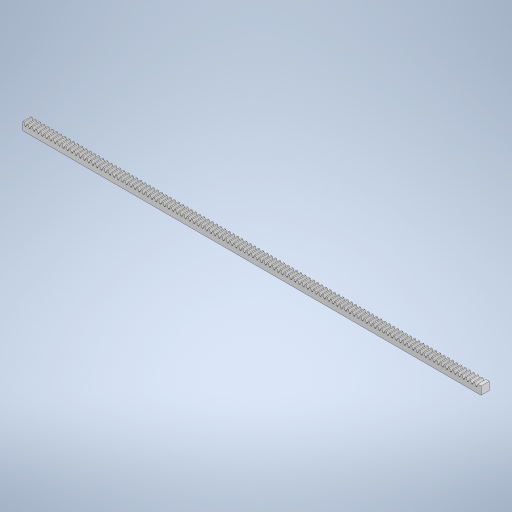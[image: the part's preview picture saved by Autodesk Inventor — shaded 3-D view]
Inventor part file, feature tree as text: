
AUTODESK INVENTOR PART (.ipt)
format: ipt  version: 2023 (Build 270158000, 158)  size: 757,248 bytes
history: mixed  units: in
note: dims shown in document units (in); Inventor stores cm internally (conversion verified against a paired STEP export)
features: extrude x1, sketch x1, other x1, imported_body x1
ambient origin geometry x8: Origin, YZ Plane, XZ Plane, XY Plane, X Axis, Y Axis, Z Axis, Center Point
bodies: Solid1 (imported_parasolid)
feature tree (4):
  extrude  "Extrusion1"  TaperAngle=0.0deg  [1 undecoded]
  sketch  "Sketch1"  dims[d0=0.05in d1=0.0in d2=0.0in]
  other  "LPattern1"
  imported_body  NMx_Import_Brep_tag  [imported B-rep: ~654 faces, bbox_mm=[180.81244, 3.175, 3.175]]
note: 1 required parameter value undecoded (feature->parameter linkage not recoverable at this tier; creation-order binding heuristic only, values carry confidence <= 0.55)
